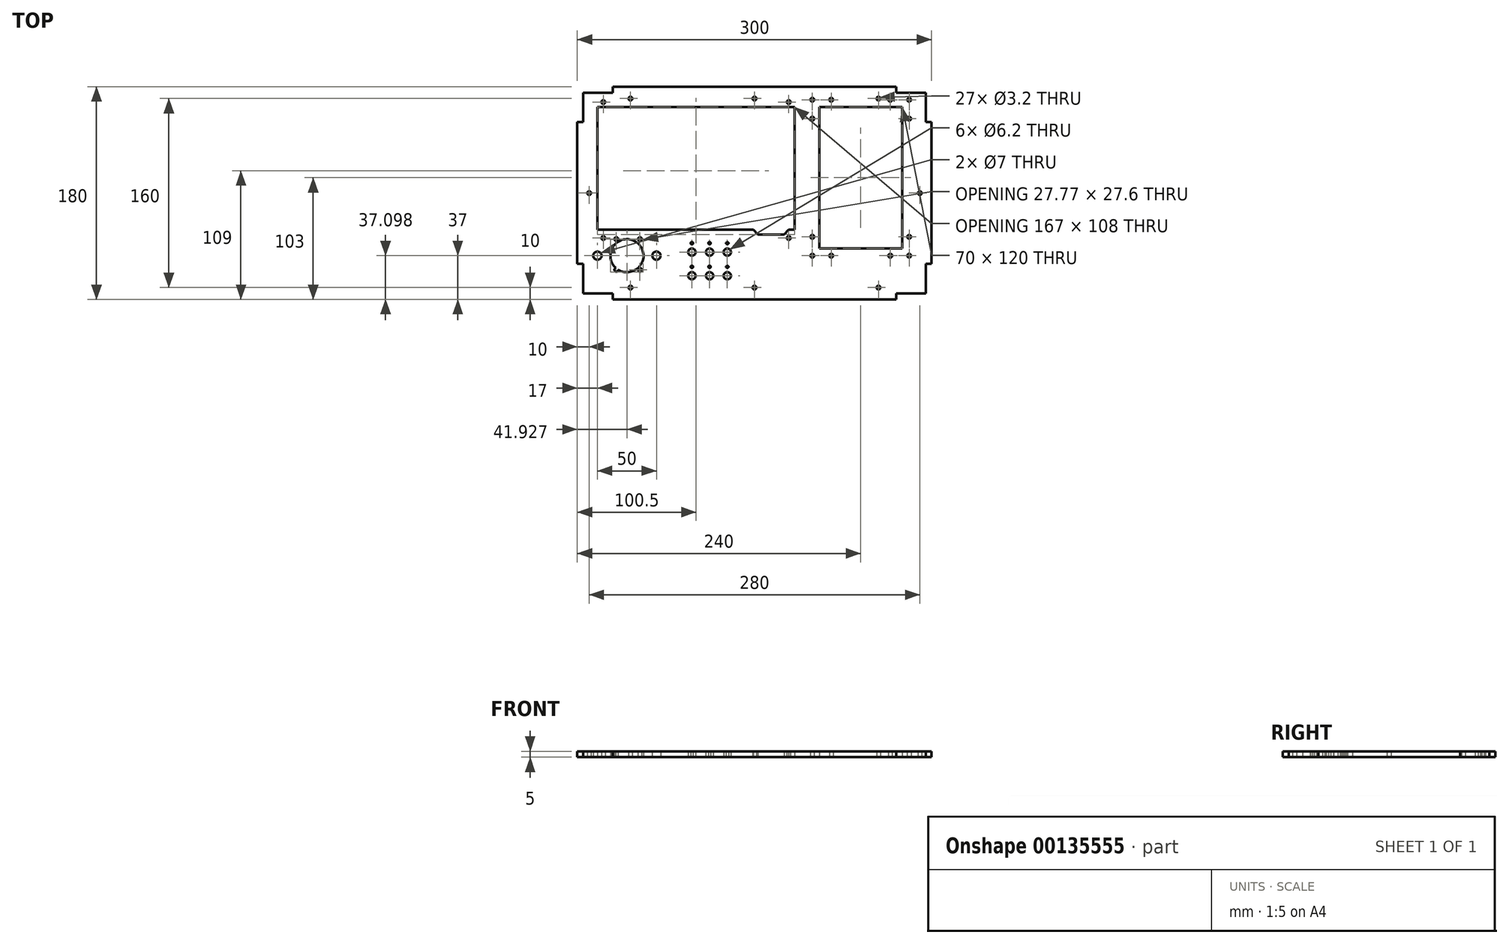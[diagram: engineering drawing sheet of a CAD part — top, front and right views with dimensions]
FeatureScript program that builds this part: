
annotation { "Feature Type Name" : "Feature", "Feature Type Description" : "" }
export const myFeature = defineFeature(function(context is Context, id is Id, definition is map)
    precondition{}
    {
        {
            var Q0;
            Q0=qCreatedBy(makeId("Top.planeOp"),FACE);
            var sketch = newSketch(context, id + "F0", { "sketchPlane" : qUnion([Q0])});
            skLineSegment(sketch, "E0", {"start": v(-150, 0) * mm, "end": v(150, 0) * mm, "construction": true});
            skLineSegment(sketch, "E1", {"start": v(0, 90) * mm, "end": v(0, -90) * mm, "construction": true});
            skLineSegment(sketch, "E2.bottom", {"start": v(-120, 90) * mm, "end": v(120, 90) * mm});
            skLineSegment(sketch, "E2.top", {"start": v(-120, -90) * mm, "end": v(120, -90) * mm});
            skLineSegment(sketch, "E2.left", {"start": v(-150, 60) * mm, "end": v(-150, -60) * mm});
            skLineSegment(sketch, "E2.right", {"start": v(150, 60) * mm, "end": v(150, -60) * mm});
            skLineSegment(sketch, "E3.bottom", {"start": v(-120, 85) * mm, "end": v(120, 85) * mm, "construction": true});
            skLineSegment(sketch, "E3.top", {"start": v(-145, -85) * mm, "end": v(145, -85) * mm, "construction": true});
            skLineSegment(sketch, "E3.left", {"start": v(-145, 60) * mm, "end": v(-145, -85) * mm, "construction": true});
            skLineSegment(sketch, "E3.right", {"start": v(145, 60) * mm, "end": v(145, -85) * mm, "construction": true});
            skLineSegment(sketch, "E4", {"start": v(-145, 85) * mm, "end": v(-120, 85) * mm});
            skLineSegment(sketch, "E5", {"start": v(-145, 85) * mm, "end": v(-145, 60) * mm});
            skLineSegment(sketch, "E6", {"start": v(-120, 85) * mm, "end": v(-120, 90) * mm});
            skLineSegment(sketch, "E7", {"start": v(-145, 60) * mm, "end": v(-150, 60) * mm});
            skLineSegment(sketch, "E8.MirrorCS", {"start": v(-120, -85) * mm, "end": v(-120, -90) * mm});
            skLineSegment(sketch, "E9.MirrorCS", {"start": v(-145, -85) * mm, "end": v(-120, -85) * mm});
            skLineSegment(sketch, "E10.MirrorCS", {"start": v(-145, -60) * mm, "end": v(-150, -60) * mm});
            skLineSegment(sketch, "E11.MirrorCS", {"start": v(-145, -85) * mm, "end": v(-145, -60) * mm});
            skLineSegment(sketch, "E12.MirrorCS", {"start": v(145, 60) * mm, "end": v(150, 60) * mm});
            skLineSegment(sketch, "E13.MirrorCS", {"start": v(145, 85) * mm, "end": v(145, 60) * mm});
            skLineSegment(sketch, "E14.MirrorCS", {"start": v(145, 85) * mm, "end": v(120, 85) * mm});
            skLineSegment(sketch, "E15.MirrorCS", {"start": v(120, 85) * mm, "end": v(120, 90) * mm});
            skLineSegment(sketch, "E16.MirrorCS", {"start": v(120, -85) * mm, "end": v(120, -90) * mm});
            skLineSegment(sketch, "E17.MirrorCS", {"start": v(145, -85) * mm, "end": v(120, -85) * mm});
            skLineSegment(sketch, "E18.MirrorCS", {"start": v(145, -85) * mm, "end": v(145, -60) * mm});
            skLineSegment(sketch, "E19.MirrorCS", {"start": v(145, -60) * mm, "end": v(150, -60) * mm});
            skLineSegment(sketch, "E20", {"start": v(-105, 107.49) * mm, "end": v(-105, -125.28) * mm, "construction": true});
            skLineSegment(sketch, "E21", {"start": v(105, 108) * mm, "end": v(105, -118.5) * mm, "construction": true});
            skLineSegment(sketch, "E22", {"start": v(-171.53, 80) * mm, "end": v(173.7, 80) * mm, "construction": true});
            skLineSegment(sketch, "E23", {"start": v(-165.8, -80) * mm, "end": v(184.12, -80) * mm, "construction": true});
            skLineSegment(sketch, "E24", {"start": v(140, 104.88) * mm, "end": v(140, -118.5) * mm, "construction": true});
            skLineSegment(sketch, "E25", {"start": v(-140, 111.65) * mm, "end": v(-140, -113.3) * mm, "construction": true});
            skCircle(sketch, "E26", {"center": v(0, 80) * mm, "radius": 1.6 * mm});
            skCircle(sketch, "E27", {"center": v(-105, 80) * mm, "radius": 1.6 * mm});
            skCircle(sketch, "E28", {"center": v(105, 80) * mm, "radius": 1.6 * mm});
            skCircle(sketch, "E29", {"center": v(140, 0) * mm, "radius": 1.6 * mm});
            skCircle(sketch, "E30", {"center": v(-140, 0) * mm, "radius": 1.6 * mm});
            skCircle(sketch, "E31", {"center": v(0, -80) * mm, "radius": 1.6 * mm});
            skCircle(sketch, "E32", {"center": v(105, -80) * mm, "radius": 1.6 * mm});
            skCircle(sketch, "E33", {"center": v(-105, -80) * mm, "radius": 1.6 * mm});
            skSolve(sketch);
        }
        {
            var Q0;
            Q0=makeQuery(id+"F0.imprint","IMPRINT",FACE,{"disambiguationData":[TD([[makeQuery(id+"F0.imprint","IMPRINT",EDGE,{"derivedFrom":sQuery(id+"F0.wireOp",EDGE,"E2.bottom")}),-1.0]])]});
            var sketch = newSketch(context, id + "F1", { "sketchPlane" : qUnion([Q0])});
            skLineSegment(sketch, "E34", {"start": v(-174.5, 21) * mm, "end": v(75.5, 21) * mm, "construction": true});
            skLineSegment(sketch, "E35", {"start": v(-49.5, 81) * mm, "end": v(-49.5, -39) * mm, "construction": true});
            skLineSegment(sketch, "E36.bottom", {"start": v(-133, 73) * mm, "end": v(34, 73) * mm});
            skLineSegment(sketch, "E36.top", {"start": v(-133, -31) * mm, "end": v(31.17, -31) * mm});
            skLineSegment(sketch, "E36.left", {"start": v(-133, 73) * mm, "end": v(-133, -31) * mm});
            skLineSegment(sketch, "E36.right", {"start": v(34, 73) * mm, "end": v(34, -31) * mm});
            skLineSegment(sketch, "E37", {"start": v(-128, 84.55) * mm, "end": v(-128, -87.13) * mm, "construction": true});
            skLineSegment(sketch, "E38", {"start": v(29, 81.55) * mm, "end": v(29, -31) * mm, "construction": true});
            skLineSegment(sketch, "E39", {"start": v(-123.03, 77) * mm, "end": v(92.2, 77) * mm, "construction": true});
            skLineSegment(sketch, "E40", {"start": v(-124.53, -38) * mm, "end": v(96.7, -38) * mm, "construction": true});
            skPoint(sketch, "E41", {"position": v(-128, 77) * mm});
            skPoint(sketch, "E42", {"position": v(29, 77) * mm});
            skPoint(sketch, "E43", {"position": v(29, -38) * mm});
            skPoint(sketch, "E44", {"position": v(-128, -38) * mm});
            skCircle(sketch, "E45", {"center": v(-128, 77) * mm, "radius": 1.6 * mm});
            skCircle(sketch, "E46", {"center": v(29, 77) * mm, "radius": 1.6 * mm});
            skCircle(sketch, "E47", {"center": v(29, -38) * mm, "radius": 1.6 * mm});
            skCircle(sketch, "E48", {"center": v(-128, -38) * mm, "radius": 1.6 * mm});
            skPoint(sketch, "E49", {"position": v(-49.5, -35) * mm});
            skLineSegment(sketch, "E50", {"start": v(28.22, -31) * mm, "end": v(31.17, -31) * mm, "construction": true});
            skLineSegment(sketch, "E51", {"start": v(28.22, -31) * mm, "end": v(34, -31) * mm});
            skLineSegment(sketch, "E52", {"start": v(3, -35) * mm, "end": v(25, -35) * mm});
            skPoint(sketch, "E53.end.orphan", {"position": v(-1, -35) * mm});
            skLineSegment(sketch, "E54.trimOffspring", {"start": v(29, -35) * mm, "end": v(29, -48.63) * mm, "construction": true});
            skLineSegment(sketch, "E55", {"start": v(25, -35) * mm, "end": v(29, -31) * mm});
            skPoint(sketch, "E56.start.orphan", {"position": v(-1, -31) * mm});
            skLineSegment(sketch, "E57", {"start": v(3, -35) * mm, "end": v(-1, -31) * mm});
            skSolve(sketch);
        }
        {
            var Q0;
            Q0=makeQuery(id+"F1.imprint","IMPRINT",FACE,{"disambiguationData":[TD([[makeQuery(id+"F1.imprint","IMPRINT",EDGE,{"derivedFrom":sQuery(id+"F1.wireOp",EDGE,"E36.bottom")}),1.0]])]});
            var sketch = newSketch(context, id + "F2", { "sketchPlane" : qUnion([Q0])});
            skLineSegment(sketch, "E58", {"start": v(90, 73.09) * mm, "end": v(90, -47.09) * mm, "construction": true});
            skLineSegment(sketch, "E59", {"start": v(-37.3, 13) * mm, "end": v(217.3, 13) * mm, "construction": true});
            skLineSegment(sketch, "E60.bottom", {"start": v(49, -53) * mm, "end": v(131, -53) * mm, "construction": true});
            skLineSegment(sketch, "E60.top", {"start": v(49, 79) * mm, "end": v(131, 79) * mm, "construction": true});
            skLineSegment(sketch, "E60.left", {"start": v(49, -53) * mm, "end": v(49, 79) * mm, "construction": true});
            skLineSegment(sketch, "E60.right", {"start": v(131, -53) * mm, "end": v(131, 79) * mm, "construction": true});
            skLineSegment(sketch, "E61.bottom", {"start": v(55, 73) * mm, "end": v(125, 73) * mm});
            skLineSegment(sketch, "E61.top", {"start": v(55, -47) * mm, "end": v(125, -47) * mm});
            skLineSegment(sketch, "E61.left", {"start": v(55, 73) * mm, "end": v(55, -47) * mm});
            skLineSegment(sketch, "E61.right", {"start": v(125, 73) * mm, "end": v(125, -47) * mm});
            skCircle(sketch, "E62", {"center": v(131, 79) * mm, "radius": 1.6 * mm});
            skCircle(sketch, "E63", {"center": v(115, 79) * mm, "radius": 1.6 * mm});
            skCircle(sketch, "E64", {"center": v(131, 63) * mm, "radius": 1.6 * mm});
            skCircle(sketch, "E65.MirrorC", {"center": v(65, 79) * mm, "radius": 1.6 * mm});
            skCircle(sketch, "E66.MirrorC", {"center": v(49, 79) * mm, "radius": 1.6 * mm});
            skCircle(sketch, "E67.MirrorC", {"center": v(49, 63) * mm, "radius": 1.6 * mm});
            skCircle(sketch, "E68.MirrorC", {"center": v(49, -37) * mm, "radius": 1.6 * mm});
            skCircle(sketch, "E69.MirrorC", {"center": v(49, -53) * mm, "radius": 1.6 * mm});
            skCircle(sketch, "E70.MirrorC", {"center": v(65, -53) * mm, "radius": 1.6 * mm});
            skCircle(sketch, "E71.MirrorC", {"center": v(115, -53) * mm, "radius": 1.6 * mm});
            skCircle(sketch, "E72.MirrorC", {"center": v(131, -53) * mm, "radius": 1.6 * mm});
            skCircle(sketch, "E73.MirrorC", {"center": v(131, -37) * mm, "radius": 1.6 * mm});
            skSolve(sketch);
        }
        {
            var Q0;
            Q0=makeQuery(id+"F0.imprint","IMPRINT",FACE,{"disambiguationData":[TD([[makeQuery(id+"F0.imprint","IMPRINT",EDGE,{"derivedFrom":sQuery(id+"F0.wireOp",EDGE,"E2.bottom")}),-1.0]])]});
            var sketch = newSketch(context, id + "F3", { "sketchPlane" : qUnion([Q0])});
            skLineSegment(sketch, "E74", {"start": v(-107, -16.34) * mm, "end": v(-107, -96.53) * mm, "construction": true});
            skLineSegment(sketch, "E75", {"start": v(-138.5, -53) * mm, "end": v(-67.25, -53) * mm, "construction": true});
            skLineSegment(sketch, "E76.bottom", {"start": v(-120, -36) * mm, "end": v(-94, -36) * mm, "construction": true});
            skLineSegment(sketch, "E76.top", {"start": v(-120, -70) * mm, "end": v(-94, -70) * mm, "construction": true});
            skLineSegment(sketch, "E76.left", {"start": v(-120, -36) * mm, "end": v(-120, -70) * mm, "construction": true});
            skLineSegment(sketch, "E76.right", {"start": v(-94, -36) * mm, "end": v(-94, -70) * mm, "construction": true});
            skLineSegment(sketch, "E77", {"start": v(-108, -22.05) * mm, "end": v(-108, -83.88) * mm, "construction": true});
            skLineSegment(sketch, "E78", {"start": v(-117, -26.34) * mm, "end": v(-117, -82.32) * mm, "construction": true});
            skLineSegment(sketch, "E79", {"start": v(-97, -25.76) * mm, "end": v(-97, -82.71) * mm, "construction": true});
            skLineSegment(sketch, "E80", {"start": v(-122.93, -39) * mm, "end": v(-61.33, -39) * mm, "construction": true});
            skLineSegment(sketch, "E81", {"start": v(-124.28, -65) * mm, "end": v(-61.33, -65) * mm, "construction": true});
            skCircle(sketch, "E82", {"center": v(-108, -53) * mm, "radius": 14 * mm});
            skCircle(sketch, "E83", {"center": v(-117, -39) * mm, "radius": 1.6 * mm});
            skCircle(sketch, "E84", {"center": v(-97, -39) * mm, "radius": 1.6 * mm});
            skCircle(sketch, "E85", {"center": v(-97, -65) * mm, "radius": 1.6 * mm});
            skCircle(sketch, "E86", {"center": v(-117, -65) * mm, "radius": 1.6 * mm});
            skPoint(sketch, "E87", {"position": v(-94, -39) * mm});
            skPoint(sketch, "E88", {"position": v(-120, -39) * mm});
            skPoint(sketch, "E89", {"position": v(-107.03, -39.03) * mm});
            skPoint(sketch, "E90", {"position": v(-81.32, -64.88) * mm});
            skPoint(sketch, "E91", {"position": v(-68.24, -64.97) * mm});
            skPoint(sketch, "E92", {"position": v(-94.47, -65) * mm});
            skPoint(sketch, "E93", {"position": v(-81.32, -53) * mm});
            skPoint(sketch, "E94", {"position": v(-170.7, -52.27) * mm});
            skCircle(sketch, "E95", {"center": v(-83, -53) * mm, "radius": 3.5 * mm});
            skCircle(sketch, "E96.MirrorC", {"center": v(-133, -53) * mm, "radius": 3.5 * mm});
            skSolve(sketch);
        }
        {
            var Q0;
            Q0=makeQuery(id+"F0.imprint","IMPRINT",FACE,{"disambiguationData":[TD([[makeQuery(id+"F0.imprint","IMPRINT",EDGE,{"derivedFrom":sQuery(id+"F0.wireOp",EDGE,"E2.bottom")}),-1.0]])]});
            var sketch = newSketch(context, id + "F4", { "sketchPlane" : qUnion([Q0])});
            skCircle(sketch, "E97", {"center": v(-53, -70) * mm, "radius": 3.1 * mm});
            skLineSegment(sketch, "E98", {"start": v(-53, -70) * mm, "end": v(-53, -62.4) * mm, "construction": true});
            skCircle(sketch, "E99", {"center": v(-53, -62.4) * mm, "radius": 1 * mm});
            skCircle(sketch, "E100.0.1.0", {"center": v(-53, -50) * mm, "radius": 3.1 * mm});
            skLineSegment(sketch, "E100.0.1.1", {"start": v(-53, -50) * mm, "end": v(-53, -42.4) * mm, "construction": true});
            skCircle(sketch, "E100.0.1.2", {"center": v(-53, -42.4) * mm, "radius": 1 * mm});
            skCircle(sketch, "E100.1.0.0", {"center": v(-38, -70) * mm, "radius": 3.1 * mm});
            skLineSegment(sketch, "E100.1.0.1", {"start": v(-38, -70) * mm, "end": v(-38, -62.4) * mm, "construction": true});
            skCircle(sketch, "E100.1.0.2", {"center": v(-38, -62.4) * mm, "radius": 1 * mm});
            skCircle(sketch, "E100.1.1.0", {"center": v(-38, -50) * mm, "radius": 3.1 * mm});
            skLineSegment(sketch, "E100.1.1.1", {"start": v(-38, -50) * mm, "end": v(-38, -42.4) * mm, "construction": true});
            skCircle(sketch, "E100.1.1.2", {"center": v(-38, -42.4) * mm, "radius": 1 * mm});
            skLineSegment(sketch, "E100.direction1", {"start": v(-53, -70) * mm, "end": v(-38, -70) * mm, "construction": true});
            skLineSegment(sketch, "E100.direction2", {"start": v(-53, -70) * mm, "end": v(-53, -50) * mm, "construction": true});
            skCircle(sketch, "E101.0.2.0", {"center": v(-23, -70) * mm, "radius": 3.1 * mm});
            skLineSegment(sketch, "E101.2.2.0", {"start": v(-23, -70) * mm, "end": v(-23, -62.4) * mm, "construction": true});
            skCircle(sketch, "E101.5.2.0", {"center": v(-23, -62.4) * mm, "radius": 1 * mm});
            skCircle(sketch, "E101.0.2.1", {"center": v(-23, -50) * mm, "radius": 3.1 * mm});
            skLineSegment(sketch, "E101.2.2.1", {"start": v(-23, -50) * mm, "end": v(-23, -42.4) * mm, "construction": true});
            skCircle(sketch, "E101.5.2.1", {"center": v(-23, -42.4) * mm, "radius": 1 * mm});
            skSolve(sketch);
        }
        {
            var Q0;
            Q0 = qSketchRegion(id + "F0", true);
            extrude(context, id + "F5", {"entities" : qUnion([Q0]), "depth" : 5 * mm});
        }
        {
            var Q0;
            Q0 = qSketchRegion(id + "F1", true);
            var Q1;
            Q1 = qSketchRegion(id + "F2", true);
            var Q2;
            Q2 = qSketchRegion(id + "F3", true);
            var Q3;
            Q3 = qSketchRegion(id + "F4", true);
            extrude(context, id + "F6", {"entities" : qUnion([Q0, Q1, Q2, Q3]), "operationType" : NewBodyOperationType.REMOVE, "depth" : 5 * mm});
        }
    });
